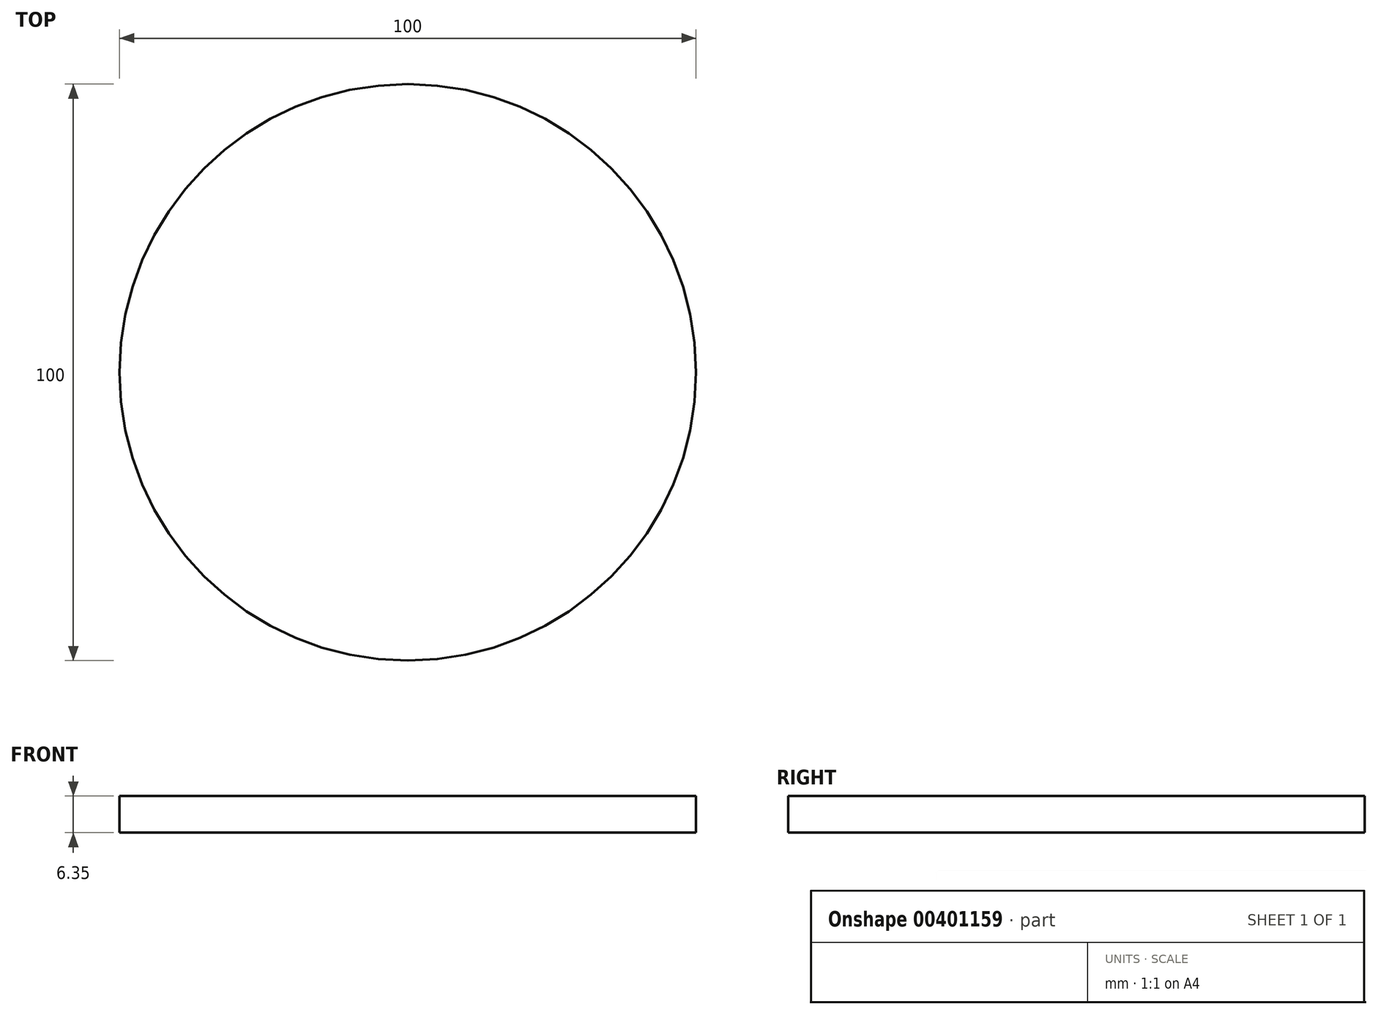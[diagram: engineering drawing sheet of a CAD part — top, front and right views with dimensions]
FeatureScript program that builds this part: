
annotation { "Feature Type Name" : "Feature", "Feature Type Description" : "" }
export const myFeature = defineFeature(function(context is Context, id is Id, definition is map)
    precondition{}
    {
        {
            var Q0;
            Q0=qCreatedBy(makeId("Top.planeOp"),FACE);
            var sketch = newSketch(context, id + "F0", { "sketchPlane" : qUnion([Q0])});
            skCircle(sketch, "E0", {"center": v(0, 0) * mm, "radius": 50 * mm});
            skSolve(sketch);
        }
        {
            var Q0;
            Q0 = qSketchRegion(id + "F0", true);
            extrude(context, id + "F1", {"entities" : qUnion([Q0]), "depth" : -6.35 * mm, "offsetDistance" : 25.4 * mm});
        }
    });
